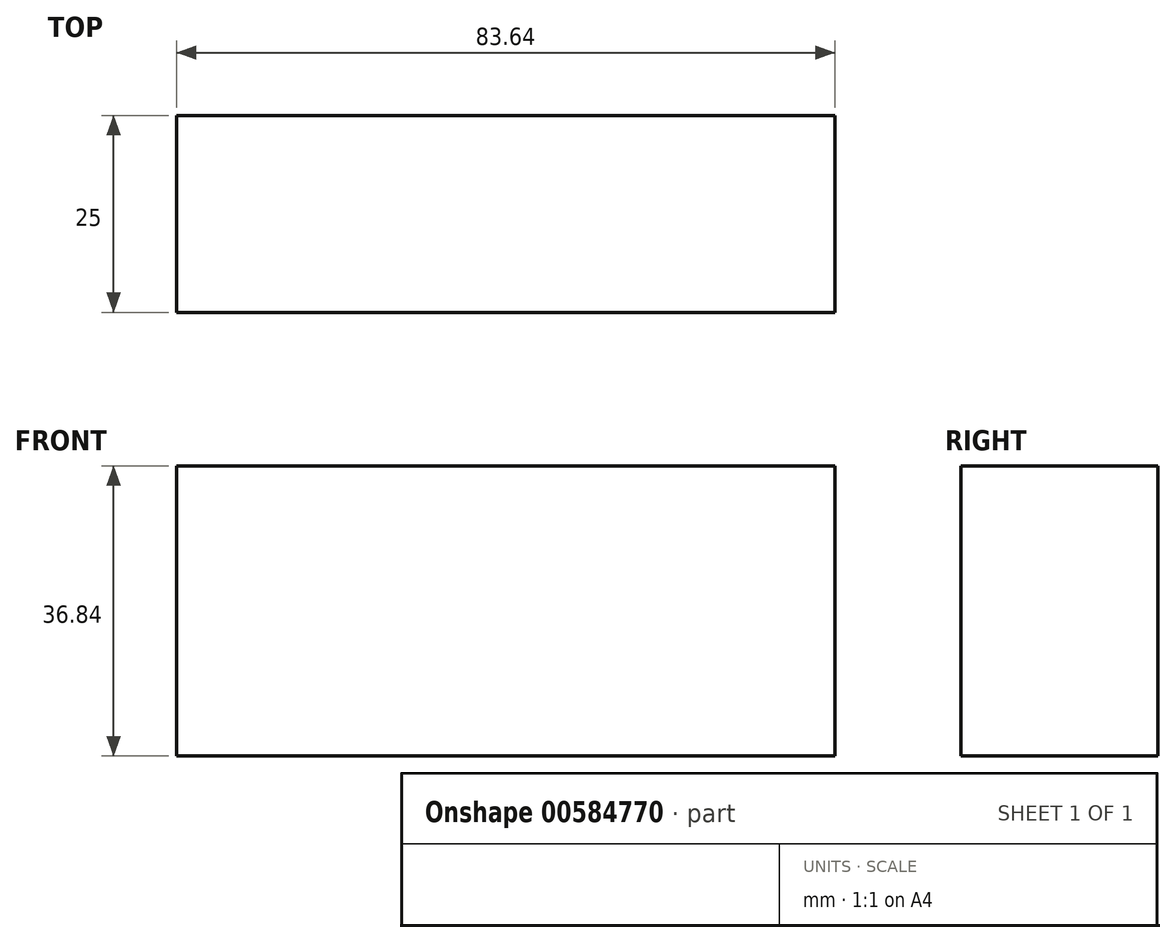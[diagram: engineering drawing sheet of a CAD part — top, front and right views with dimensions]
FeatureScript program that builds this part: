
annotation { "Feature Type Name" : "Feature", "Feature Type Description" : "" }
export const myFeature = defineFeature(function(context is Context, id is Id, definition is map)
    precondition{}
    {
        {
            var Q0;
            Q0=qCreatedBy(makeId("Front.planeOp"),FACE);
            var sketch = newSketch(context, id + "F0", { "sketchPlane" : qUnion([Q0])});
            skLineSegment(sketch, "E0.bottom", {"start": v(-47.63, 33.15) * mm, "end": v(36.01, 33.15) * mm});
            skLineSegment(sketch, "E0.top", {"start": v(-47.63, -3.7) * mm, "end": v(36.01, -3.7) * mm});
            skLineSegment(sketch, "E0.left", {"start": v(-47.63, 33.15) * mm, "end": v(-47.63, -3.7) * mm});
            skLineSegment(sketch, "E0.right", {"start": v(36.01, 33.15) * mm, "end": v(36.01, -3.7) * mm});
            skSolve(sketch);
        }
        {
            var Q0;
            Q0=makeQuery(id+"F0.imprint","IMPRINT",FACE,{"disambiguationData":[TD([[makeQuery(id+"F0.imprint","IMPRINT",EDGE,{"derivedFrom":sQuery(id+"F0.wireOp",EDGE,"E0.bottom")}),-1.0]])]});
            extrude(context, id + "F1", {"entities" : qUnion([Q0]), "depth" : 25 * mm, "offsetDistance" : 25 * mm});
        }
    });
